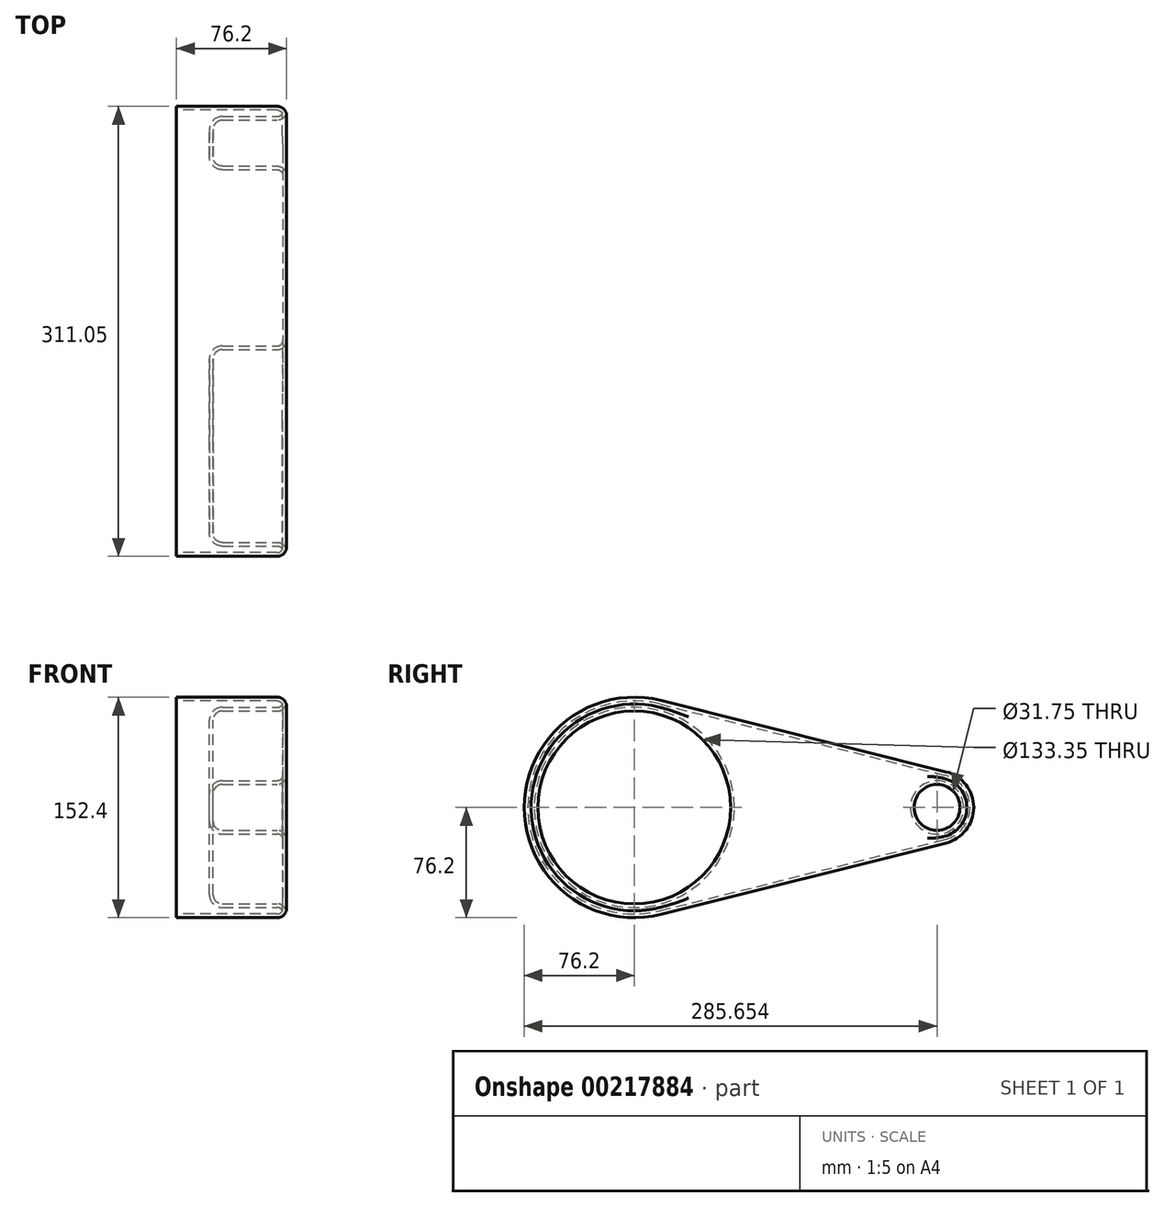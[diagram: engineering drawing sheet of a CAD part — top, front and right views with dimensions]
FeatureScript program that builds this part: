
annotation { "Feature Type Name" : "Feature", "Feature Type Description" : "" }
export const myFeature = defineFeature(function(context is Context, id is Id, definition is map)
    precondition{}
    {
        {
            var Q0;
            Q0=qCreatedBy(makeId("Right.planeOp"),FACE);
            var sketch = newSketch(context, id + "F0", { "sketchPlane" : qUnion([Q0])});
            skCircle(sketch, "E0", {"center": v(0, 0) * mm, "radius": 76.2 * mm});
            skCircle(sketch, "E1", {"center": v(209.45, 0) * mm, "radius": 25.4 * mm});
            skLineSegment(sketch, "E2", {"start": v(18.48, 73.92) * mm, "end": v(215.61, 24.64) * mm});
            skLineSegment(sketch, "E3", {"start": v(18.48, -73.92) * mm, "end": v(215.61, -24.64) * mm});
            skSolve(sketch);
        }
        {
            var Q0;
            {var subQ0=sQuery(id+"F0.wireOp",EDGE,"E0");var subQ1=makeQuery(id+"F0.imprint","INTERSECT",VERTEX,{"derivedFrom":[subQ0,sQuery(id+"F0.wireOp",EDGE,"E2")]});Q0=makeQuery(id+"F0.imprint","IMPRINT",FACE,{"disambiguationData":[TD([[makeQuery(id+"F0.imprint","IMPRINT",EDGE,{"disambiguationData":[TD([[subQ1,-1.0]])],"derivedFrom":subQ0}),1.0]])]});}
            var Q1;
            {var subQ0=sQuery(id+"F0.wireOp",EDGE,"E2");Q1=makeQuery(id+"F0.imprint","IMPRINT",FACE,{"disambiguationData":[TD([[makeQuery(id+"F0.imprint","IMPRINT",EDGE,{"derivedFrom":subQ0}),-1.0]])]});}
            var Q2;
            {var subQ0=sQuery(id+"F0.wireOp",EDGE,"E1");var subQ1=makeQuery(id+"F0.imprint","INTERSECT",VERTEX,{"derivedFrom":[subQ0,sQuery(id+"F0.wireOp",EDGE,"E2")]});Q2=makeQuery(id+"F0.imprint","IMPRINT",FACE,{"disambiguationData":[TD([[makeQuery(id+"F0.imprint","IMPRINT",EDGE,{"disambiguationData":[TD([[subQ1,-1.0]])],"derivedFrom":subQ0}),1.0]])]});}
            extrude(context, id + "F1", {"entities" : qUnion([Q0, Q1, Q2]), "depth" : 76.2 * mm});
        }
        {
            var Q0;
            Q0=makeQuery(id+"F1.opExtrude","CAP_FACE",FACE,{"disambiguationData":[OSD([sQuery(id+"F0.wireOp",EDGE,"E0"),sQuery(id+"F0.wireOp",EDGE,"E1"),sQuery(id+"F0.wireOp",EDGE,"E2"),sQuery(id+"F0.wireOp",EDGE,"E3")])],"isStart":false});
            var sketch = newSketch(context, id + "F2", { "sketchPlane" : qUnion([Q0])});
            skCircle(sketch, "E4", {"center": v(0, 0) * mm, "radius": 66.68 * mm});
            skCircle(sketch, "E5", {"center": v(209.45, 0) * mm, "radius": 15.88 * mm});
            skSolve(sketch);
        }
        {
            var Q0;
            Q0=makeQuery(id+"F2.imprint","IMPRINT",FACE,{"disambiguationData":[TD([[makeQuery(id+"F2.imprint","IMPRINT",EDGE,{"derivedFrom":sQuery(id+"F2.wireOp",EDGE,"E4")}),1.0]])]});
            var Q1;
            Q1=makeQuery(id+"F2.imprint","IMPRINT",FACE,{"disambiguationData":[TD([[makeQuery(id+"F2.imprint","IMPRINT",EDGE,{"derivedFrom":sQuery(id+"F2.wireOp",EDGE,"E5")}),1.0]])]});
            extrude(context, id + "F3", {"entities" : qUnion([Q0, Q1]), "operationType" : NewBodyOperationType.REMOVE, "oppositeDirection" : true, "depth" : 50.8 * mm});
        }
        {
            var Q0;
            Q0=makeQuery(id+"F1.opExtrude","CAP_FACE",FACE,{"disambiguationData":[OSD([sQuery(id+"F0.wireOp",EDGE,"E0"),sQuery(id+"F0.wireOp",EDGE,"E1"),sQuery(id+"F0.wireOp",EDGE,"E2"),sQuery(id+"F0.wireOp",EDGE,"E3")])],"isStart":false});
            var Q1;
            Q1=makeQuery(id+"F3.boolean.opBoolean","COPY",EDGE,{"derivedFrom":makeQuery(id+"F3.opExtrude","CAP_EDGE",EDGE,{"disambiguationData":[OSD([sQuery(id+"F2.wireOp",EDGE,"E4")])],"isStart":false})});
            var Q2;
            Q2=makeQuery(id+"F3.boolean.opBoolean","COPY",FACE,{"derivedFrom":makeQuery(id+"F3.opExtrude","CAP_FACE",FACE,{"disambiguationData":[OSD([sQuery(id+"F2.wireOp",EDGE,"E5")])],"isStart":false})});
            fillet(context, id + "F4", {"entities" : qUnion([Q0, Q1, Q2]), "radius" : 6.35 * mm, "tangentPropagation" : true, "allowEdgeOverflow" : false});
        }
        {
            var Q0;
            Q0=makeQuery(id+"F1.opExtrude","CAP_FACE",FACE,{"disambiguationData":[OSD([sQuery(id+"F0.wireOp",EDGE,"E0"),sQuery(id+"F0.wireOp",EDGE,"E1"),sQuery(id+"F0.wireOp",EDGE,"E2"),sQuery(id+"F0.wireOp",EDGE,"E3")])],"isStart":true});
            shell(context, id + "F5", {"entities" : qUnion([Q0]), "thickness" : 2.54 * mm});
        }
    });
